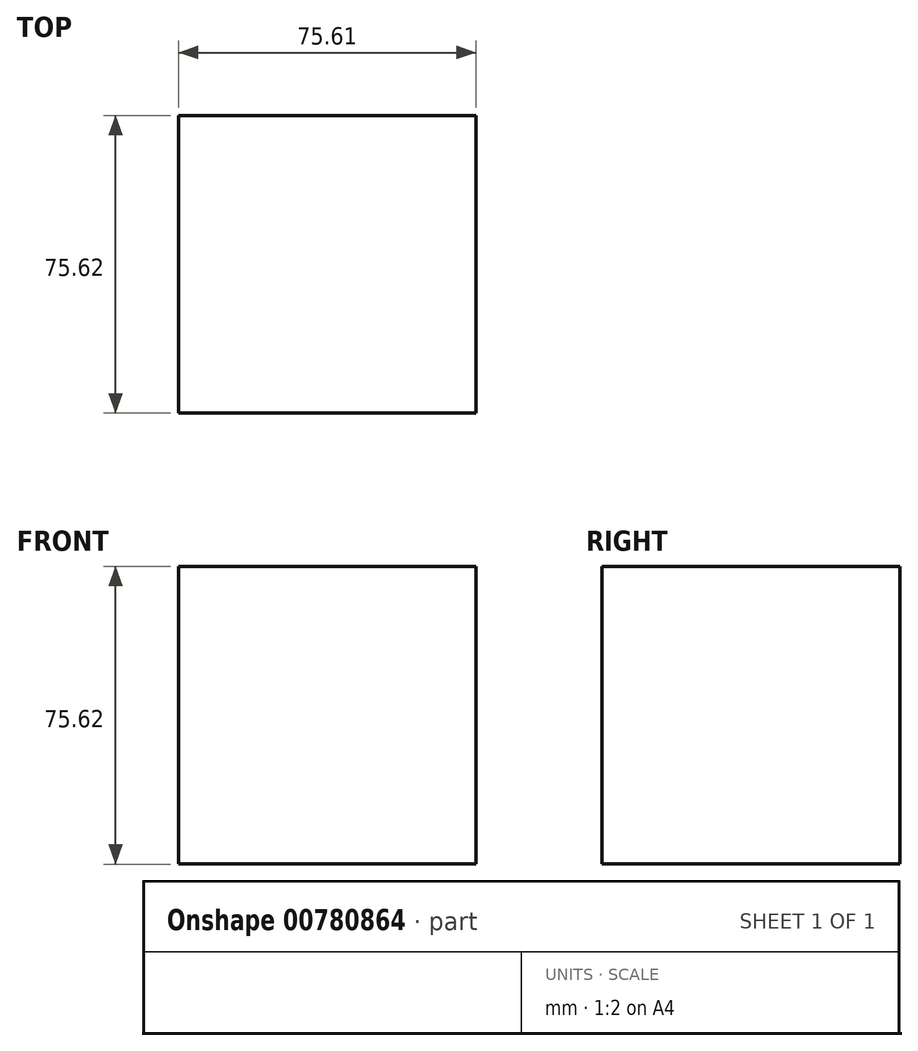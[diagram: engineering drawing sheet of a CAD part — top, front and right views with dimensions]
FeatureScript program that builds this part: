
annotation { "Feature Type Name" : "Feature", "Feature Type Description" : "" }
export const myFeature = defineFeature(function(context is Context, id is Id, definition is map)
    precondition{}
    {
        {
            var Q0;
            Q0=qCreatedBy(makeId("Front.planeOp"),FACE);
            var sketch = newSketch(context, id + "F0", { "sketchPlane" : qUnion([Q0])});
            skLineSegment(sketch, "E0.bottom", {"start": v(-36.71, 37.8) * mm, "end": v(38.9, 37.8) * mm});
            skLineSegment(sketch, "E0.top", {"start": v(-36.71, -37.8) * mm, "end": v(38.9, -37.8) * mm});
            skLineSegment(sketch, "E0.left", {"start": v(-36.71, 37.8) * mm, "end": v(-36.71, -37.8) * mm});
            skLineSegment(sketch, "E0.right", {"start": v(38.9, 37.8) * mm, "end": v(38.9, -37.8) * mm});
            skPoint(sketch, "E0.middle", {"position": v(1.1, 0) * mm});
            skSolve(sketch);
        }
        {
            var Q0;
            Q0 = qSketchRegion(id + "F0", true);
            extrude(context, id + "F1", {"entities" : qUnion([Q0]), "depth" : 75.62 * mm, "offsetDistance" : 25.4 * mm});
        }
    });
